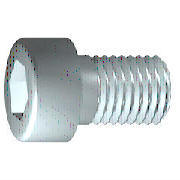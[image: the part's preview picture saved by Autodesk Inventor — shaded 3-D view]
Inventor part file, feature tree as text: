
AUTODESK INVENTOR PART (.ipt)
format: ipt  version: 2016 (Build 200138000, 138)  size: 194,048 bytes
history: native  units: mm (DEFAULTED — no unit token found)
features: sketch x2, extrude x1, plane x1, fillet x1
ambient origin geometry x7: Origin, YZ Plane, XY Plane, X Axis, Y Axis, Z Axis, Center Point
bodies: Solid1 (feature_tree), Body (feature_tree)
feature tree (5):
  extrude  "Slot"  Depth=5.0mm
  plane  "Work Plane1"
  fillet  "Fillet2"  Radius=5.0mm
  sketch  "Sketch1"  dims[d1=23.0mm d2=0.49086mm d3=5.0mm]
  sketch  "Sketch2"  dims[d4=2.5mm d5=60.0deg d6=5.0mm d7=5.0mm d8=4.618802mm d9=8.5mm d10=90.0deg d11=10.0mm d12=0.0mm d13=23.0mm d14=0.0mm d15=0.49076mm d16=0.49076mm d17=0.5mm d19=0.0mm d26=25.0mm d27=45.0deg d28=0.0mm d29=0.0mm d30=0.1mm]
